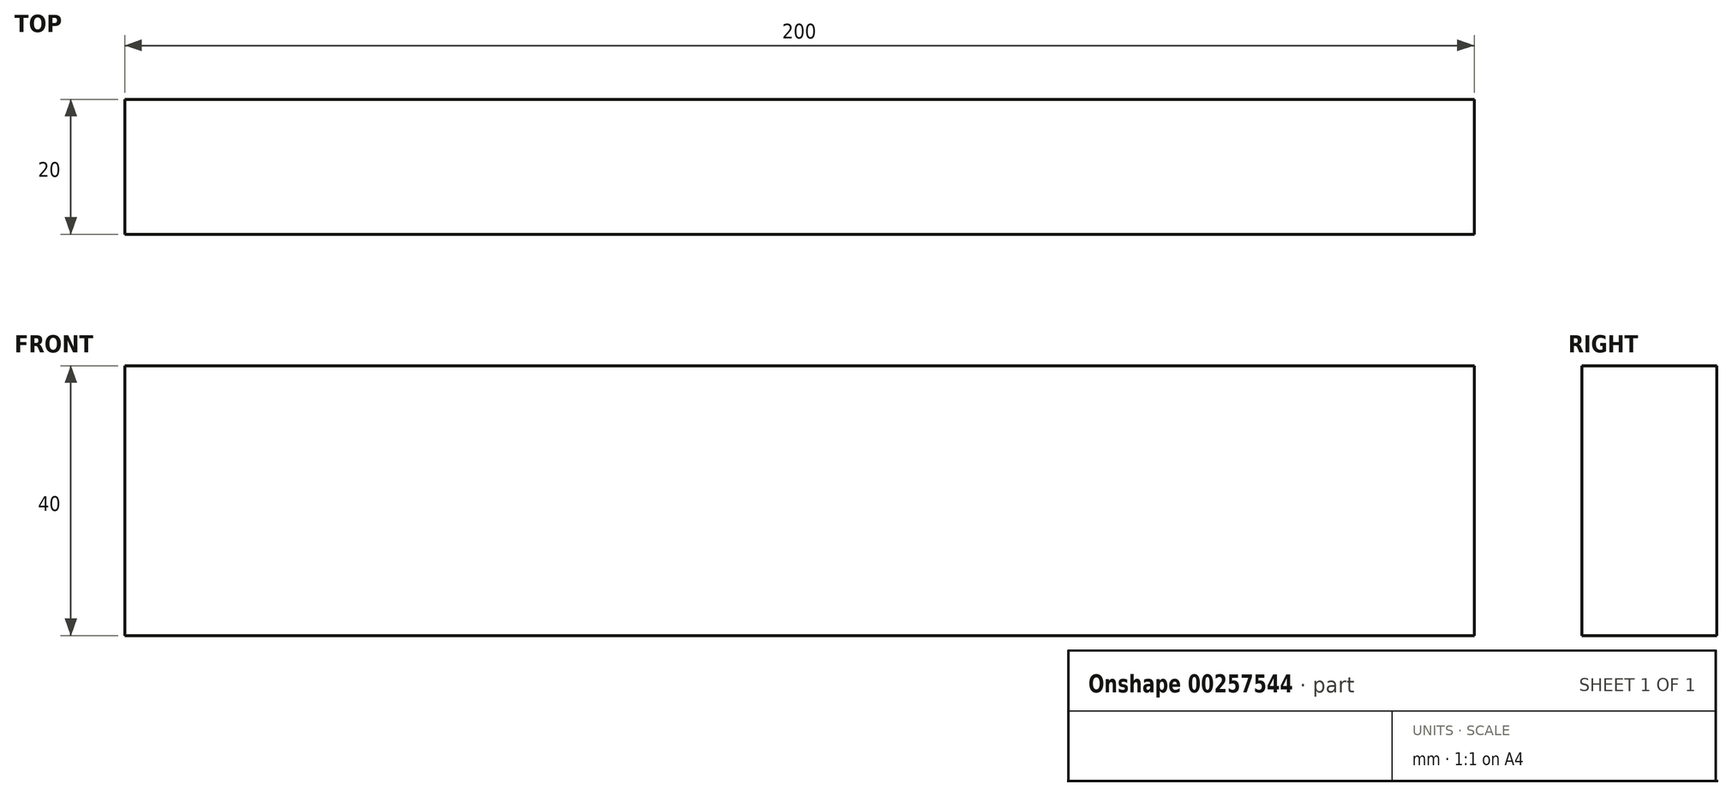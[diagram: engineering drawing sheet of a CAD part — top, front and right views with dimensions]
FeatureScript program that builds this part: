
annotation { "Feature Type Name" : "Feature", "Feature Type Description" : "" }
export const myFeature = defineFeature(function(context is Context, id is Id, definition is map)
    precondition{}
    {
        {
            var Q0;
            Q0=qCreatedBy(makeId("Right.planeOp"),FACE);
            var sketch = newSketch(context, id + "F0", { "sketchPlane" : qUnion([Q0])});
            skLineSegment(sketch, "E0.bottom", {"start": v(56.35, -20) * mm, "end": v(76.35, -20) * mm});
            skLineSegment(sketch, "E0.top", {"start": v(56.35, 20) * mm, "end": v(76.35, 20) * mm});
            skLineSegment(sketch, "E0.left", {"start": v(56.35, -20) * mm, "end": v(56.35, 20) * mm});
            skLineSegment(sketch, "E0.right", {"start": v(76.35, -20) * mm, "end": v(76.35, 20) * mm});
            skPoint(sketch, "E0.middle", {"position": v(66.35, 0) * mm});
            skSolve(sketch);
        }
        {
            var Q0;
            Q0=makeQuery(id+"F0.imprint","IMPRINT",FACE,{"disambiguationData":[TD([[makeQuery(id+"F0.imprint","IMPRINT",EDGE,{"derivedFrom":sQuery(id+"F0.wireOp",EDGE,"E0.bottom")}),1.0]])]});
            extrude(context, id + "F1", {"entities" : qUnion([Q0]), "depth" : 200 * mm});
        }
    });
